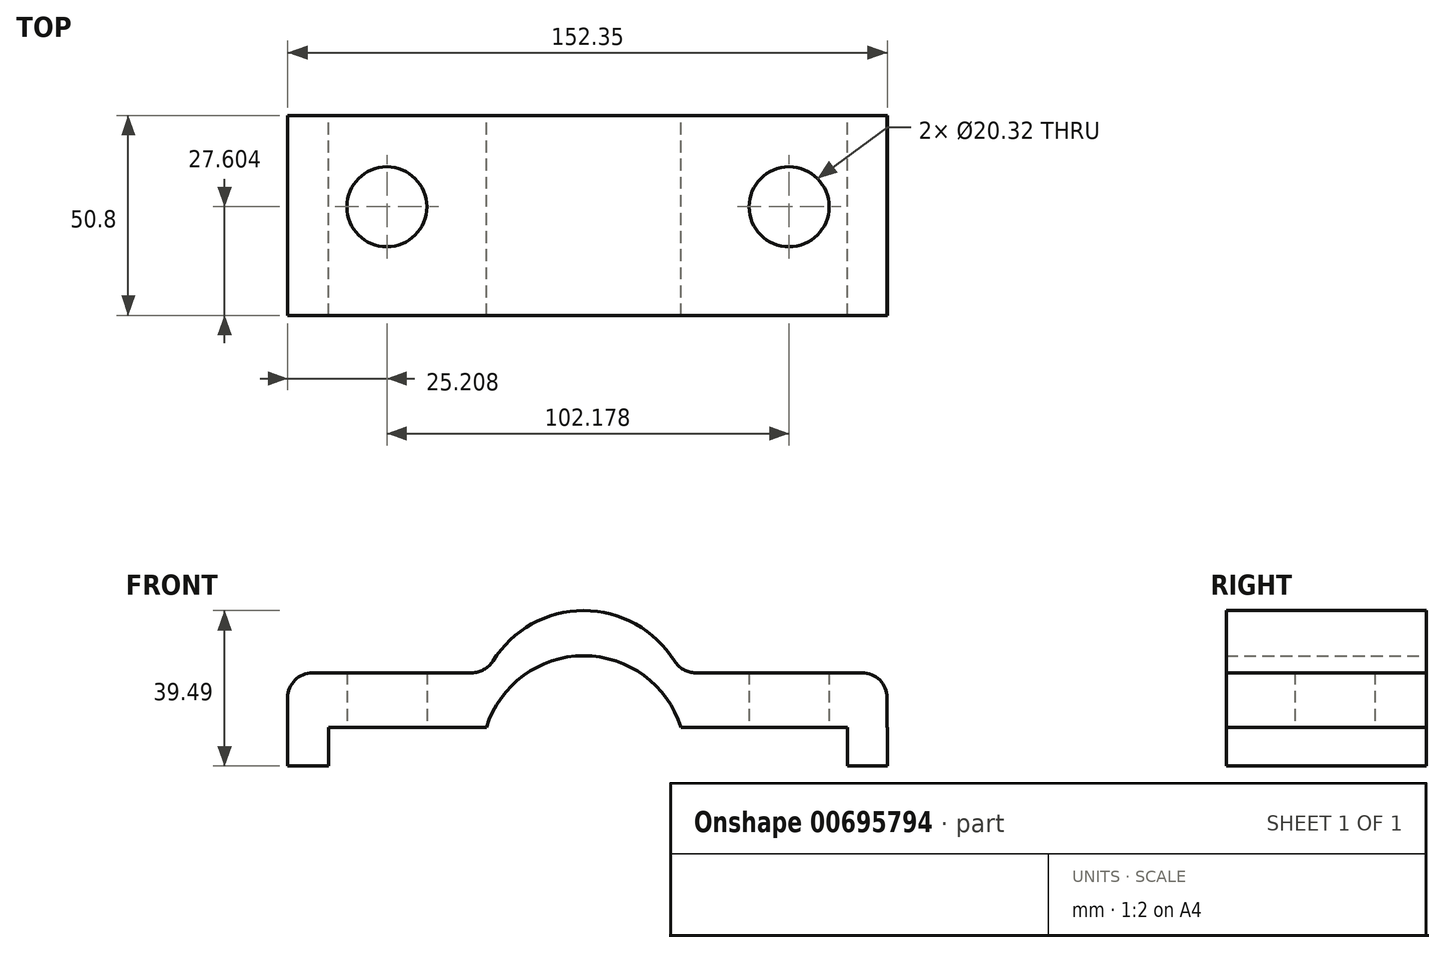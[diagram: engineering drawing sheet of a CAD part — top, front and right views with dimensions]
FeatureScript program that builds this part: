
annotation { "Feature Type Name" : "Feature", "Feature Type Description" : "" }
export const myFeature = defineFeature(function(context is Context, id is Id, definition is map)
    precondition{}
    {
        {
            var Q0;
            Q0=qCreatedBy(makeId("Front.planeOp"),FACE);
            var sketch = newSketch(context, id + "F0", { "sketchPlane" : qUnion([Q0])});
            skArc(sketch, "E0", {"start": v(23.75, 0) * mm, "mid": v(-0.95, 18.19) * mm, "end": v(-25.64, 0) * mm});
            skLineSegment(sketch, "E1", {"start": v(-76.15, 0) * mm, "end": v(-76.2, 0) * mm});
            skLineSegment(sketch, "E2.top", {"start": v(-29.4, 13.87) * mm, "end": v(-69.8, 13.87) * mm});
            skLineSegment(sketch, "E2.right", {"start": v(-76.15, 0) * mm, "end": v(-76.15, 7.52) * mm});
            skLineSegment(sketch, "E3.top", {"start": v(27.52, 13.87) * mm, "end": v(69.8, 13.87) * mm});
            skLineSegment(sketch, "E3.right", {"start": v(76.15, 0) * mm, "end": v(76.15, 7.52) * mm});
            skArc(sketch, "E4", {"start": v(22.13, 16.86) * mm, "mid": v(-0.95, 29.66) * mm, "end": v(-24.02, 16.86) * mm});
            skPoint(sketch, "E5.visualSharp", {"position": v(-25.64, 13.87) * mm});
            skArc(sketch, "E5.filletArc", {"start": v(-29.4, 13.87) * mm, "mid": v(-26.33, 14.67) * mm, "end": v(-24.02, 16.86) * mm});
            skPoint(sketch, "E6.visualSharp", {"position": v(23.75, 13.87) * mm});
            skArc(sketch, "E6.filletArc", {"start": v(22.13, 16.86) * mm, "mid": v(24.44, 14.67) * mm, "end": v(27.52, 13.87) * mm});
            skLineSegment(sketch, "E7.top", {"start": v(-76.15, -9.83) * mm, "end": v(-65.75, -9.83) * mm});
            skLineSegment(sketch, "E7.left", {"start": v(-76.15, 0) * mm, "end": v(-76.15, -9.83) * mm});
            skLineSegment(sketch, "E7.right", {"start": v(-65.75, 0) * mm, "end": v(-65.75, -9.83) * mm});
            skLineSegment(sketch, "E8.bottom", {"start": v(76.2, 0) * mm, "end": v(76.15, 0) * mm});
            skLineSegment(sketch, "E8.top", {"start": v(76.2, -9.83) * mm, "end": v(66.03, -9.83) * mm});
            skLineSegment(sketch, "E8.left", {"start": v(76.2, 0) * mm, "end": v(76.2, -9.83) * mm});
            skLineSegment(sketch, "E8.right", {"start": v(66.03, 0) * mm, "end": v(66.03, -9.83) * mm});
            skLineSegment(sketch, "E9.trimOffspring", {"start": v(76.15, 0) * mm, "end": v(76.2, 0) * mm});
            skLineSegment(sketch, "E10", {"start": v(-65.75, 0) * mm, "end": v(-25.64, 0) * mm});
            skLineSegment(sketch, "E11", {"start": v(23.75, 0) * mm, "end": v(66.03, 0) * mm});
            skPoint(sketch, "E12.visualSharp", {"position": v(-76.15, 13.87) * mm});
            skArc(sketch, "E12.filletArc", {"start": v(-69.8, 13.87) * mm, "mid": v(-74.29, 12.01) * mm, "end": v(-76.15, 7.52) * mm});
            skPoint(sketch, "E13.visualSharp", {"position": v(76.15, 13.87) * mm});
            skArc(sketch, "E13.filletArc", {"start": v(76.15, 7.52) * mm, "mid": v(74.29, 12.01) * mm, "end": v(69.8, 13.87) * mm});
            skSolve(sketch);
        }
        {
            var Q0;
            Q0 = qSketchRegion(id + "F0", true);
            extrude(context, id + "F1", {"entities" : qUnion([Q0]), "depth" : 50.8 * mm, "offsetDistance" : 25.4 * mm});
        }
        {
            var Q0;
            Q0=qCreatedBy(makeId("Top.planeOp"),FACE);
            var sketch = newSketch(context, id + "F2", { "sketchPlane" : qUnion([Q0])});
            skCircle(sketch, "E14", {"center": v(-50.94, -23.2) * mm, "radius": 10.6 * mm});
            skCircle(sketch, "E15", {"center": v(51.24, -23.2) * mm, "radius": 9.97 * mm});
            skSolve(sketch);
        }
        {
            var Q0;
            Q0=sQuery(id+"F2.wireOp",VERTEX,"E14.center");
            var Q1;
            Q1=sQuery(id+"F2.wireOp",VERTEX,"E15.center");
            var Q2;
            Q2=makeQuery(id+"F1.opExtrude","SWEPT_BODY",BODY,{"disambiguationData":[OSD([sQuery(id+"F0.wireOp",EDGE,"E0"),sQuery(id+"F0.wireOp",EDGE,"E2.top"),sQuery(id+"F0.wireOp",EDGE,"E2.right"),sQuery(id+"F0.wireOp",EDGE,"E3.top"),sQuery(id+"F0.wireOp",EDGE,"E3.right"),sQuery(id+"F0.wireOp",EDGE,"E4"),sQuery(id+"F0.wireOp",EDGE,"E5.filletArc"),sQuery(id+"F0.wireOp",EDGE,"E6.filletArc"),sQuery(id+"F0.wireOp",EDGE,"E7.top"),sQuery(id+"F0.wireOp",EDGE,"E7.left"),sQuery(id+"F0.wireOp",EDGE,"E7.right"),sQuery(id+"F0.wireOp",EDGE,"E8.top"),sQuery(id+"F0.wireOp",EDGE,"E8.left"),sQuery(id+"F0.wireOp",EDGE,"E8.right"),sQuery(id+"F0.wireOp",EDGE,"E9.trimOffspring"),sQuery(id+"F0.wireOp",EDGE,"E10"),sQuery(id+"F0.wireOp",EDGE,"E11"),sQuery(id+"F0.wireOp",EDGE,"E12.filletArc"),sQuery(id+"F0.wireOp",EDGE,"E13.filletArc")])]});
            hole(context, id + "F3", {"style" : HoleStyle.SIMPLE, "endStyle" : HoleEndStyle.THROUGH, "oppositeDirection" : true, "holeDiameter" : 20.32 * mm, "majorDiameter" : 6.35 * mm, "isTappedThrough" : true, "tappedDepth" : 12.7 * mm, "tapClearance" : 3, "locations" : qUnion([Q0, Q1]), "scope" : qUnion([Q2])});
        }
    });
